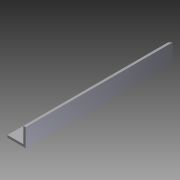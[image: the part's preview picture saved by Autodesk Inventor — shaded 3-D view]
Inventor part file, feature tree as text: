
AUTODESK INVENTOR PART (.ipt)
format: ipt  version: 2012 (Build 160160000, 160)  size: 91,648 bytes
history: native  units: in
note: dims shown in document units (in); Inventor stores cm internally (conversion verified against a paired STEP export)
features: extrude x3, sketch x3
ambient origin geometry x8: Origin, YZ Plane, XZ Plane, XY Plane, X Axis, Y Axis, Z Axis, Center Point
bodies: Solid1 (feature_tree)
feature tree (6):
  extrude  "Extrusion1"  Depth=1.0in
  extrude  "Extrusion2"  Depth=0.125in
  extrude  "Extrusion3"  TaperAngle=45.0deg  [1 undecoded]
  sketch  "Sketch1"  dims[d0=1.0in d1=1.0in]
  sketch  "Sketch2"  dims[d2=0.125in d3=0.125in]
  sketch  "Sketch3"  dims[d4=8.125in d5=0.0in d8=45.0deg d9=8.0in d10=0.0in d11=0.25in d12=4.5in d13=0.375in d14=1.0in d15=0.0in]
note: 1 required parameter value undecoded (feature->parameter linkage not recoverable at this tier; creation-order binding heuristic only, values carry confidence <= 0.55)
